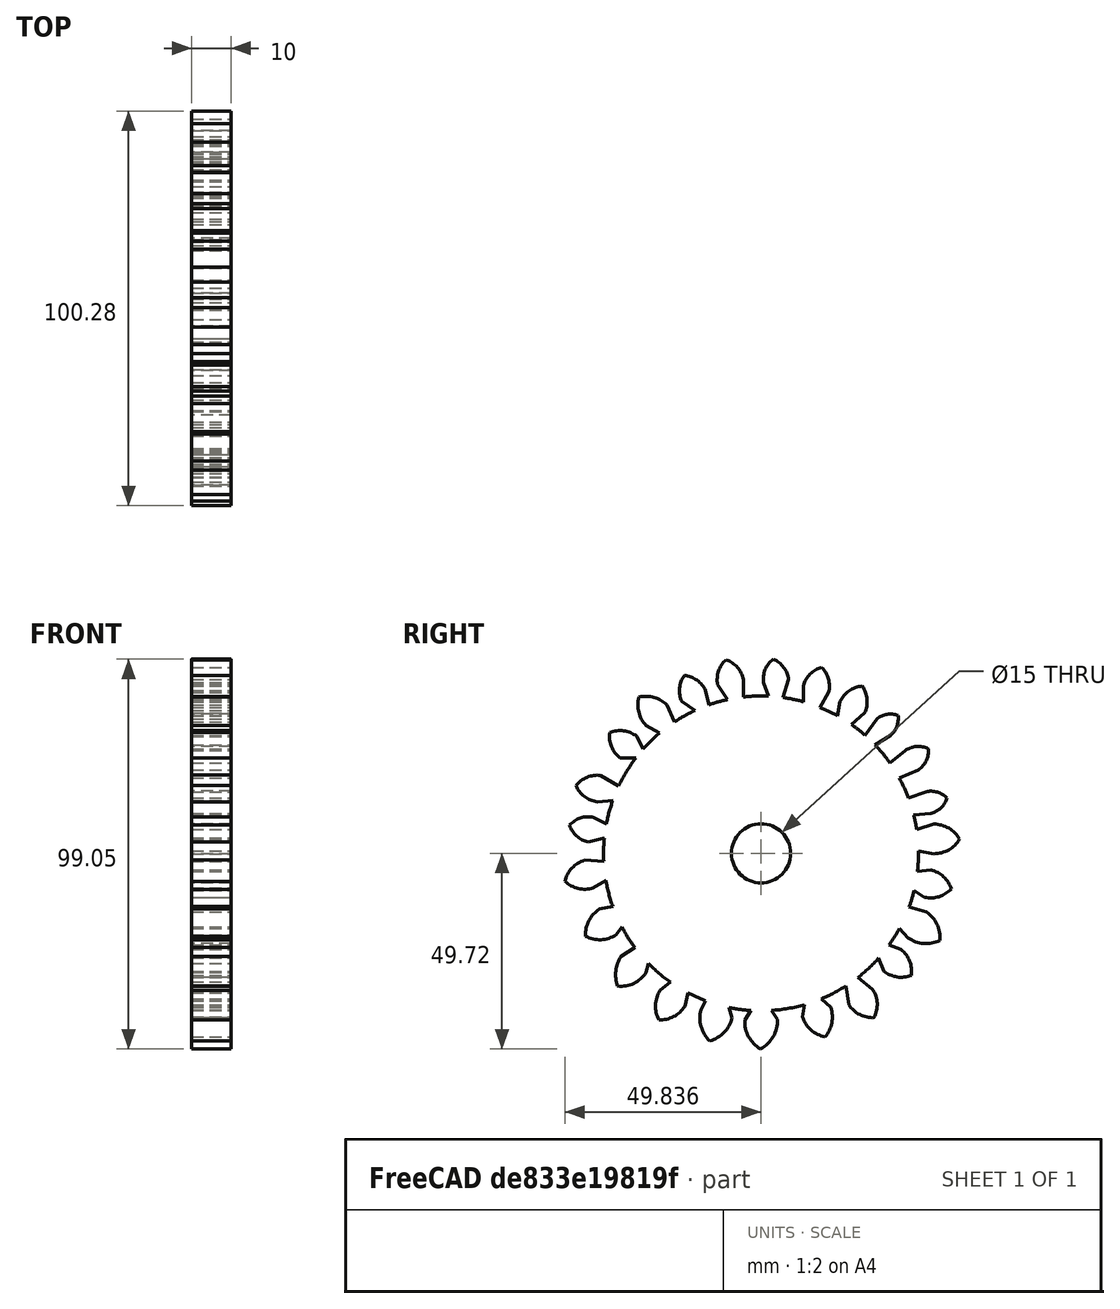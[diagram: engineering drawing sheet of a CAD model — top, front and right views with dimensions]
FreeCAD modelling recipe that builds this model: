
FCSTD DOCUMENT  (FreeCAD 0.21R33771 (Git))
Label: Machine Elment Design3
License: All rights reserved
LicenseURL: http://en.wikipedia.org/wiki/All_rights_reserved
objects: Sketcher::SketchObject×1, PartDesign::Pad×1, PartDesign::Body×1
note: 4 computed .brp shape members not serialized (recipe doc carries the construction recipe); baked Part::Feature solids carry a one-line shape summary decoded from their .brp

FEATURE [Sketcher::SketchObject] Sketch002
  FullyConstrained = false
  MapMode = 5
  Placement = pos=(0,0,0) rot=(0.57735,0.57735,0.57735;2.0944rad)
  Support = -> [YZ_Plane001]
  sketch-geometry (121):
    g0: Circle CenterX=-9.99419 CenterY=-0.180247 CenterZ=0 NormalX=0 NormalY=0 NormalZ=1 AngleXU=0 Radius=7.5
    g1: ArcOfCircle CenterX=-9.99419 CenterY=-0.180247 CenterZ=0 NormalX=0 NormalY=0 NormalZ=1 AngleXU=0 Radius=40 StartAngle=4.77797 EndAngle=4.99193
    g2: LineSegment StartX=4.94728 StartY=36.9244 StartZ=0 EndX=7.1719 EndY=40.7061 EndZ=0
    g3: LineSegment StartX=0.780338 StartY=38.3413 StartZ=0 EndX=0.755399 EndY=42.3758 EndZ=0
    g4: LineSegment StartX=-8.16746 StartY=39.778 StartZ=0 EndX=-9.38573 EndY=43.1826 EndZ=0
    g5: LineSegment StartX=-4.4803 StartY=39.4379 StartZ=0 EndX=-2.97992 EndY=44.0138 EndZ=0
    g6: LineSegment StartX=9.43345 StartY=34.785 StartZ=0 EndX=10.0579 EndY=38.368 EndZ=0
    g7: LineSegment StartX=12.9649 StartY=32.5746 StartZ=0 EndX=16.32 EndY=35.4471 EndZ=0
    g8: LineSegment StartX=16.4407 StartY=29.8397 StartZ=0 EndX=19.4768 EndY=34.0249 EndZ=0
    g9: LineSegment StartX=18.9896 StartY=27.3867 StartZ=0 EndX=22.8597 EndY=29.824 EndZ=0
    g10: LineSegment StartX=22.7265 StartY=22.8275 StartZ=0 EndX=26.6327 EndY=25.969 EndZ=0
    g11: LineSegment StartX=25.142 StartY=18.9364 StartZ=0 EndX=29.9678 EndY=21.0695 EndZ=0
    g12: LineSegment StartX=27.436 StartY=13.9257 StartZ=0 EndX=31.8669 EndY=15.4629 EndZ=0
    g13: LineSegment StartX=28.7806 StartY=9.64413 StartZ=0 EndX=33.1773 EndY=10.0099 EndZ=0
    g14: LineSegment StartX=29.5451 StartY=5.87322 StartZ=0 EndX=33.9689 EndY=7.25486 EndZ=0
    g15: LineSegment StartX=30.0003 StartY=0.485889 StartZ=0 EndX=33.9215 EndY=-0.257635 EndZ=0
    g16: LineSegment StartX=29.7446 StartY=-4.74416 StartZ=0 EndX=33.1412 EndY=-4.39115 EndZ=0
    g17: LineSegment StartX=28.8747 StartY=-9.62515 StartZ=0 EndX=31.5488 EndY=-11.3142 EndZ=0
    g18: LineSegment StartX=27.6371 StartY=-13.7408 StartZ=0 EndX=31.9739 EndY=-14.9902 EndZ=0
    g19: LineSegment StartX=25.1392 StartY=-19.3021 StartZ=0 EndX=27.3595 EndY=-21.6696 EndZ=0
    g20: LineSegment StartX=22.519 StartY=-23.4803 StartZ=0 EndX=25.6088 EndY=-24.633 EndZ=0
    g21: LineSegment StartX=19.8821 StartY=-26.7774 StartZ=0 EndX=21.2196 EndY=-30.1223 EndZ=0
    g22: LineSegment StartX=14.6541 StartY=-31.6836 StartZ=0 EndX=18.3711 EndY=-34.7285 EndZ=0
    g23: LineSegment StartX=11.6058 StartY=-33.8469 StartZ=0 EndX=12.3333 EndY=-38.6399 EndZ=0
    g24: LineSegment StartX=5.32297 StartY=-37.1314 StartZ=0 EndX=7.74528 EndY=-39.3474 EndZ=0
    g25: LineSegment StartX=1.04227 StartY=-38.6276 StartZ=0 EndX=0.551182 EndY=-41.7728 EndZ=0
    g26: LineSegment StartX=-18.1954 StartY=-39.3305 StartZ=0 EndX=-17.322 EndY=-41.9506 EndZ=0
    g27: LineSegment StartX=-24.0726 StartY=-37.6208 StartZ=0 EndX=-25.2906 EndY=-39.9483 EndZ=0
    g28: LineSegment StartX=-28.5263 StartY=-35.6283 StartZ=0 EndX=-29.3648 EndY=-39.0464 EndZ=0
    g29: LineSegment StartX=-33.0173 StartY=-32.8901 StartZ=0 EndX=-35.6372 EndY=-35.0452 EndZ=0
    g30: LineSegment StartX=-42.076 StartY=-24.0707 StartZ=0 EndX=-45.563 EndY=-26.3582 EndZ=0
    g31: LineSegment StartX=-45.3496 StartY=-18.8885 StartZ=0 EndX=-46.8081 EndY=-20.9017 EndZ=0
    g32: LineSegment StartX=-47.6402 StartY=-13.6999 StartZ=0 EndX=-50.9826 EndY=-14.2983 EndZ=0
    g33: LineSegment StartX=-49.4096 StartY=-6.99361 StartZ=0 EndX=-52.6314 EndY=-8.96467 EndZ=0
    g34: LineSegment StartX=-49.944 StartY=-2.18408 StartZ=0 EndX=-54.7931 EndY=-1.89974 EndZ=0
    g35: LineSegment StartX=-49.8015 StartY=3.7408 StartZ=0 EndX=-53.8673 EndY=2.70363 EndZ=0
    g36: LineSegment StartX=-49.2916 StartY=7.28397 StartZ=0 EndX=-52.5325 EndY=8.9854 EndZ=0
    g37: LineSegment StartX=-47.6693 StartY=13.258 StartZ=0 EndX=-51.6018 EndY=12.9345 EndZ=0
    g38: LineSegment StartX=-46.1533 StartY=16.9229 StartZ=0 EndX=-50.742 EndY=19.6321 EndZ=0
    g39: LineSegment StartX=-35.8355 StartY=30.3522 StartZ=0 EndX=-39.184 EndY=32.334 EndZ=0
    g40: LineSegment StartX=-31.9684 StartY=33.2433 StartZ=0 EndX=-33.8705 EndY=37.4981 EndZ=0
    g41: LineSegment StartX=-39.9365 StartY=26.3425 StartZ=0 EndX=-41.575 EndY=29.5668 EndZ=0
    g42: LineSegment StartX=-41.7916 StartY=24.0875 StartZ=0 EndX=-45.7975 EndY=24.0875 EndZ=0
    g43: LineSegment StartX=-26.7619 StartY=36.1356 StartZ=0 EndX=-30.1078 EndY=38.3785 EndZ=0
    g44: LineSegment StartX=-23.241 StartY=37.5626 StartZ=0 EndX=-24.0609 EndY=41.1716 EndZ=0
    g45: LineSegment StartX=-18.484 StartY=38.9084 StartZ=0 EndX=-21.0175 EndY=42.7184 EndZ=0
    g46: LineSegment StartX=-14.4903 StartY=39.5663 StartZ=0 EndX=-14.4903 EndY=43.9875 EndZ=0
    g47: ArcOfCircle CenterX=-9.38573 CenterY=43.1826 CenterZ=0 NormalX=0 NormalY=0 NormalZ=1 AngleXU=0 Radius=6.45951 StartAngle=0.129034 EndAngle=1.17623
    g48: ArcOfCircle CenterX=0.755399 CenterY=42.3758 CenterZ=0 NormalX=0 NormalY=0 NormalZ=1 AngleXU=0 Radius=6.63017 StartAngle=6.02862 EndAngle=7.07582
    g49: ArcOfCircle CenterX=10.0579 CenterY=38.368 CenterZ=0 NormalX=0 NormalY=0 NormalZ=1 AngleXU=0 Radius=6.90983 StartAngle=5.84675 EndAngle=6.89395
    g50: ArcOfCircle CenterX=19.4768 CenterY=34.0249 CenterZ=0 NormalX=0 NormalY=0 NormalZ=1 AngleXU=0 Radius=5.39369 StartAngle=5.39034 EndAngle=6.43754
    g51: ArcOfCircle CenterX=-21.0175 CenterY=42.7184 CenterZ=0 NormalX=0 NormalY=0 NormalZ=1 AngleXU=0 Radius=6.64951 StartAngle=0.192033 EndAngle=1.23923
    g52: ArcOfCircle CenterX=-30.1078 CenterY=38.3785 CenterZ=0 NormalX=0 NormalY=0 NormalZ=1 AngleXU=0 Radius=6.66085 StartAngle=0.43272 EndAngle=1.47992
    g53: ArcOfCircle CenterX=-39.184 CenterY=32.334 CenterZ=0 NormalX=0 NormalY=0 NormalZ=1 AngleXU=0 Radius=7.40955 StartAngle=0.77115 EndAngle=1.81835
    g54: ArcOfCircle CenterX=-45.7975 CenterY=24.0875 CenterZ=0 NormalX=0 NormalY=0 NormalZ=1 AngleXU=0 Radius=6.91758 StartAngle=0.914224 EndAngle=1.96142
    g55: ArcOfCircle CenterX=-51.6018 CenterY=12.9345 CenterZ=0 NormalX=0 NormalY=0 NormalZ=1 AngleXU=0 Radius=6.7525 StartAngle=1.44313 EndAngle=2.49033
    g56: ArcOfCircle CenterX=26.6327 CenterY=25.969 CenterZ=0 NormalX=0 NormalY=0 NormalZ=1 AngleXU=0 Radius=5.92692 StartAngle=5.31005 EndAngle=6.35725
    g57: ArcOfCircle CenterX=31.8669 CenterY=15.4629 CenterZ=0 NormalX=0 NormalY=0 NormalZ=1 AngleXU=0 Radius=5.60822 StartAngle=4.94823 EndAngle=5.99543
    g58: ArcOfCircle CenterX=33.9689 CenterY=7.25486 CenterZ=0 NormalX=0 NormalY=0 NormalZ=1 AngleXU=0 Radius=7.51265 StartAngle=4.70608 EndAngle=5.75328
    g59: ArcOfCircle CenterX=33.1412 CenterY=-4.39115 CenterZ=0 NormalX=0 NormalY=0 NormalZ=1 AngleXU=0 Radius=7.10381 StartAngle=4.4863 EndAngle=5.5335
    g60: ArcOfCircle CenterX=31.9739 CenterY=-14.9902 CenterZ=0 NormalX=0 NormalY=0 NormalZ=1 AngleXU=0 Radius=8.11826 StartAngle=4.10784 EndAngle=5.15504
    g61: ArcOfCircle CenterX=25.6088 CenterY=-24.633 CenterZ=0 NormalX=0 NormalY=0 NormalZ=1 AngleXU=0 Radius=7.02836 StartAngle=4.0379 EndAngle=5.0851
    g62: ArcOfCircle CenterX=18.3711 CenterY=-34.7285 CenterZ=0 NormalX=0 NormalY=0 NormalZ=1 AngleXU=0 Radius=7.19398 StartAngle=3.71643 EndAngle=4.76363
    g63: ArcOfCircle CenterX=-5.78085 CenterY=-42.7894 CenterZ=0 NormalX=0 NormalY=0 NormalZ=1 AngleXU=0 Radius=8.35625 StartAngle=3.11136 EndAngle=4.15955
    g64: ArcOfCircle CenterX=-17.322 CenterY=-41.9506 CenterZ=0 NormalX=0 NormalY=0 NormalZ=1 AngleXU=0 Radius=8.21631 StartAngle=2.89542 EndAngle=3.94262
    g65: ArcOfCircle CenterX=-29.3648 CenterY=-39.0464 CenterZ=0 NormalX=0 NormalY=0 NormalZ=1 AngleXU=0 Radius=7.43996 StartAngle=2.57377 EndAngle=3.62096
    g66: ArcOfCircle CenterX=-38.5302 CenterY=-30.9575 CenterZ=0 NormalX=0 NormalY=0 NormalZ=1 AngleXU=0 Radius=8.4032 StartAngle=2.56243 EndAngle=3.49802
    g67: ArcOfCircle CenterX=-46.8081 CenterY=-20.9017 CenterZ=0 NormalX=0 NormalY=0 NormalZ=1 AngleXU=0 Radius=7.8123 StartAngle=2.13454 EndAngle=3.18173
    g68: ArcOfCircle CenterX=-52.6314 CenterY=-8.96467 CenterZ=0 NormalX=0 NormalY=0 NormalZ=1 AngleXU=0 Radius=7.38824 StartAngle=1.86773 EndAngle=2.91493
    g69: ArcOfCircle CenterX=-53.8673 CenterY=2.70363 CenterZ=0 NormalX=0 NormalY=0 NormalZ=1 AngleXU=0 Radius=6.42202 StartAngle=1.36141 EndAngle=2.40861
    g70: LineSegment StartX=-38.6225 StartY=-28.1162 StartZ=0 EndX=-39.1898 EndY=-30.4587 EndZ=0
    g71: LineSegment StartX=-7.37288 StartY=-40.0943 StartZ=0 EndX=-5.77157 EndY=-42.3697 EndZ=0
    g72: LineSegment StartX=-12.554 StartY=-40.0983 StartZ=0 EndX=-14.1333 EndY=-42.5369 EndZ=0
    g73: ArcOfCircle CenterX=-9.99419 CenterY=-0.180247 CenterZ=0 NormalX=0 NormalY=0 NormalZ=1 AngleXU=0 Radius=40 StartAngle=5.10535 EndAngle=5.28282
    g74: ArcOfCircle CenterX=-9.99419 CenterY=-0.180247 CenterZ=0 NormalX=0 NormalY=0 NormalZ=1 AngleXU=0 Radius=40 StartAngle=5.37631 EndAngle=5.55579
    g75: ArcOfCircle CenterX=-9.99419 CenterY=-0.180247 CenterZ=0 NormalX=0 NormalY=0 NormalZ=1 AngleXU=0 Radius=40 StartAngle=5.66138 EndAngle=5.78476
    g76: ArcOfCircle CenterX=-9.99419 CenterY=-0.180247 CenterZ=0 NormalX=0 NormalY=0 NormalZ=1 AngleXU=0 Radius=40 StartAngle=5.93732 EndAngle=6.04481
    g77: ArcOfCircle CenterX=-9.99419 CenterY=-0.180247 CenterZ=0 NormalX=0 NormalY=0 NormalZ=1 AngleXU=0 Radius=40 StartAngle=6.16884 EndAngle=6.29984
    g78: ArcOfCircle CenterX=-9.99419 CenterY=-0.180247 CenterZ=0 NormalX=0 NormalY=0 NormalZ=1 AngleXU=0 Radius=40 StartAngle=1.29806 EndAngle=1.43251
    g79: ArcOfCircle CenterX=-9.99419 CenterY=-0.180247 CenterZ=0 NormalX=0 NormalY=0 NormalZ=1 AngleXU=0 Radius=40 StartAngle=1.06364 EndAngle=1.18798
    g80: ArcOfCircle CenterX=-9.99419 CenterY=-0.180247 CenterZ=0 NormalX=0 NormalY=0 NormalZ=1 AngleXU=0 Radius=40 StartAngle=1.52511 EndAngle=1.68344
    g81: ArcOfCircle CenterX=-9.99419 CenterY=-0.180247 CenterZ=0 NormalX=0 NormalY=0 NormalZ=1 AngleXU=0 Radius=40 StartAngle=1.78467 EndAngle=1.90834
    g82: ArcOfCircle CenterX=-9.99419 CenterY=-0.180247 CenterZ=0 NormalX=0 NormalY=0 NormalZ=1 AngleXU=0 Radius=40 StartAngle=0.848816 EndAngle=0.959442
    g83: ArcOfCircle CenterX=-9.99419 CenterY=-0.180247 CenterZ=0 NormalX=0 NormalY=0 NormalZ=1 AngleXU=0 Radius=40 StartAngle=0.612841 EndAngle=0.76035
    g84: ArcOfCircle CenterX=-9.99419 CenterY=-0.180247 CenterZ=0 NormalX=0 NormalY=0 NormalZ=1 AngleXU=0 Radius=40 StartAngle=0.360399 EndAngle=0.498281
    g85: ArcOfCircle CenterX=-9.99419 CenterY=-0.180247 CenterZ=0 NormalX=0 NormalY=0 NormalZ=1 AngleXU=0 Radius=40 StartAngle=0.15192 EndAngle=0.248148
    g86: ArcOfCircle CenterX=-9.99419 CenterY=-0.180247 CenterZ=0 NormalX=0 NormalY=0 NormalZ=1 AngleXU=0 Radius=40 StartAngle=4.5059 EndAngle=4.64835
    g87: ArcOfCircle CenterX=-9.99419 CenterY=-0.180247 CenterZ=0 NormalX=0 NormalY=0 NormalZ=1 AngleXU=0 Radius=40 StartAngle=4.23067 EndAngle=4.35272
    g88: ArcOfCircle CenterX=-9.99419 CenterY=-0.180247 CenterZ=0 NormalX=0 NormalY=0 NormalZ=1 AngleXU=0 Radius=40 StartAngle=3.91475 EndAngle=4.09908
    g89: ArcOfCircle CenterX=-9.99419 CenterY=-0.180247 CenterZ=0 NormalX=0 NormalY=0 NormalZ=1 AngleXU=0 Radius=40 StartAngle=3.62829 EndAngle=3.78168
    g90: ArcOfCircle CenterX=-9.99419 CenterY=-0.180247 CenterZ=0 NormalX=0 NormalY=0 NormalZ=1 AngleXU=0 Radius=40 StartAngle=3.31276 EndAngle=3.48637
    g91: ArcOfCircle CenterX=-9.99419 CenterY=-0.180247 CenterZ=0 NormalX=0 NormalY=0 NormalZ=1 AngleXU=0 Radius=40 StartAngle=3.04341 EndAngle=3.19171
    g92: ArcOfCircle CenterX=-9.99419 CenterY=-0.180247 CenterZ=0 NormalX=0 NormalY=0 NormalZ=1 AngleXU=0 Radius=40 StartAngle=2.79897 EndAngle=2.95389
    g93: ArcOfCircle CenterX=-9.99419 CenterY=-0.180247 CenterZ=0 NormalX=0 NormalY=0 NormalZ=1 AngleXU=0 Radius=40 StartAngle=2.4897 EndAngle=2.69978
    g94: ArcOfCircle CenterX=-9.99419 CenterY=-0.180247 CenterZ=0 NormalX=0 NormalY=0 NormalZ=1 AngleXU=0 Radius=40 StartAngle=2.27317 EndAngle=2.41668
    g95: ArcOfCircle CenterX=-9.99419 CenterY=-0.180247 CenterZ=0 NormalX=0 NormalY=0 NormalZ=1 AngleXU=0 Radius=40 StartAngle=2.00335 EndAngle=2.15239
    g96: ArcOfCircle CenterX=7.74528 CenterY=-39.3474 CenterZ=0 NormalX=0 NormalY=0 NormalZ=1 AngleXU=0 Radius=7.59194 StartAngle=3.46676 EndAngle=4.51396
    g97: ArcOfCircle CenterX=-24.0609 CenterY=41.1716 CenterZ=0 NormalX=0 NormalY=0 NormalZ=1 AngleXU=0 Radius=6.66085 StartAngle=2.52712 EndAngle=3.57431
    g98: ArcOfCircle CenterX=-14.4903 CenterY=43.9875 CenterZ=0 NormalX=0 NormalY=0 NormalZ=1 AngleXU=0 Radius=6.64951 StartAngle=2.28643 EndAngle=3.33363
    g99: ArcOfCircle CenterX=-2.97992 CenterY=44.0138 CenterZ=0 NormalX=0 NormalY=0 NormalZ=1 AngleXU=0 Radius=6.45951 StartAngle=2.22343 EndAngle=3.27063
    g100: ArcOfCircle CenterX=7.1719 CenterY=40.7061 CenterZ=0 NormalX=0 NormalY=0 NormalZ=1 AngleXU=0 Radius=6.63017 StartAngle=1.83983 EndAngle=2.88703
    g101: ArcOfCircle CenterX=16.32 CenterY=35.4471 CenterZ=0 NormalX=0 NormalY=0 NormalZ=1 AngleXU=0 Radius=6.90983 StartAngle=1.65796 EndAngle=2.70516
    g102: ArcOfCircle CenterX=22.8597 CenterY=29.824 CenterZ=0 NormalX=0 NormalY=0 NormalZ=1 AngleXU=0 Radius=5.39369 StartAngle=1.20155 EndAngle=2.24875
    g103: ArcOfCircle CenterX=29.9678 CenterY=21.0695 CenterZ=0 NormalX=0 NormalY=0 NormalZ=1 AngleXU=0 Radius=5.92692 StartAngle=1.12126 EndAngle=2.16846
    g104: ArcOfCircle CenterX=33.1773 CenterY=10.0099 CenterZ=0 NormalX=0 NormalY=0 NormalZ=1 AngleXU=0 Radius=5.60822 StartAngle=0.75944 EndAngle=1.80664
    g105: ArcOfCircle CenterX=33.9215 CenterY=-0.257635 CenterZ=0 NormalX=0 NormalY=0 NormalZ=1 AngleXU=0 Radius=7.51265 StartAngle=0.517294 EndAngle=1.56449
    g106: ArcOfCircle CenterX=31.5488 CenterY=-11.3142 CenterZ=0 NormalX=0 NormalY=0 NormalZ=1 AngleXU=0 Radius=7.10381 StartAngle=0.297513 EndAngle=1.34471
    g107: ArcOfCircle CenterX=27.3595 CenterY=-21.6696 CenterZ=0 NormalX=0 NormalY=0 NormalZ=1 AngleXU=0 Radius=8.11826 StartAngle=6.20224 EndAngle=7.24944
    g108: ArcOfCircle CenterX=21.2196 CenterY=-30.1223 CenterZ=0 NormalX=0 NormalY=0 NormalZ=1 AngleXU=0 Radius=7.02836 StartAngle=6.1323 EndAngle=7.1795
    g109: ArcOfCircle CenterX=12.3333 CenterY=-38.6399 CenterZ=0 NormalX=0 NormalY=0 NormalZ=1 AngleXU=0 Radius=7.19398 StartAngle=5.81083 EndAngle=6.85802
    g110: ArcOfCircle CenterX=0.551182 CenterY=-41.7728 CenterZ=0 NormalX=0 NormalY=0 NormalZ=1 AngleXU=0 Radius=7.59194 StartAngle=5.56116 EndAngle=6.60836
    g111: ArcOfCircle CenterX=-14.1333 CenterY=-42.5369 CenterZ=0 NormalX=0 NormalY=0 NormalZ=1 AngleXU=0 Radius=8.36339 StartAngle=5.20625 EndAngle=6.30317
    g112: ArcOfCircle CenterX=-25.2906 CenterY=-39.9483 CenterZ=0 NormalX=0 NormalY=0 NormalZ=1 AngleXU=0 Radius=8.21631 StartAngle=4.98982 EndAngle=6.03702
    g113: ArcOfCircle CenterX=-35.6372 CenterY=-35.0452 CenterZ=0 NormalX=0 NormalY=0 NormalZ=1 AngleXU=0 Radius=7.43996 StartAngle=4.66816 EndAngle=5.71536
    g114: ArcOfCircle CenterX=-45.563 CenterY=-26.3582 CenterZ=0 NormalX=0 NormalY=0 NormalZ=1 AngleXU=0 Radius=7.57838 StartAngle=4.60102 EndAngle=5.71147
    g115: ArcOfCircle CenterX=-50.9826 CenterY=-14.2983 CenterZ=0 NormalX=0 NormalY=0 NormalZ=1 AngleXU=0 Radius=7.8123 StartAngle=4.22893 EndAngle=5.27613
    g116: ArcOfCircle CenterX=-54.7931 CenterY=-1.89974 CenterZ=0 NormalX=0 NormalY=0 NormalZ=1 AngleXU=0 Radius=7.38824 StartAngle=3.96212 EndAngle=5.00932
    g117: ArcOfCircle CenterX=-33.8705 CenterY=37.4981 CenterZ=0 NormalX=0 NormalY=0 NormalZ=1 AngleXU=0 Radius=7.40955 StartAngle=2.86554 EndAngle=3.91274
    g118: ArcOfCircle CenterX=-41.575 CenterY=29.5668 CenterZ=0 NormalX=0 NormalY=0 NormalZ=1 AngleXU=0 Radius=6.91758 StartAngle=3.00862 EndAngle=4.05582
    g119: ArcOfCircle CenterX=-50.742 CenterY=19.6321 CenterZ=0 NormalX=0 NormalY=0 NormalZ=1 AngleXU=0 Radius=6.7525 StartAngle=3.53752 EndAngle=4.58472
    g120: ArcOfCircle CenterX=-52.5325 CenterY=8.9854 CenterZ=0 NormalX=0 NormalY=0 NormalZ=1 AngleXU=0 Radius=6.42202 StartAngle=3.45581 EndAngle=4.50301
  constraints (261):
    c: Diameter(g0) = 15
    c: Coincident(g1,g0)
    c: Diameter(g1) = 80
    c: PointOnObject(g2,g1)
    c: PointOnObject(g3,g1)
    c: PointOnObject(g4,g1)
    c: PointOnObject(g5,g1)
    c: PointOnObject(g6,g1)
    c: PointOnObject(g7,g1)
    c: PointOnObject(g8,g1)
    c: PointOnObject(g9,g1)
    c: PointOnObject(g10,g1)
    c: PointOnObject(g11,g1)
    c: PointOnObject(g12,g1)
    c: PointOnObject(g13,g1)
    c: PointOnObject(g14,g1)
    c: PointOnObject(g15,g1)
    c: PointOnObject(g16,g1)
    c: PointOnObject(g17,g1)
    c: PointOnObject(g18,g1)
    c: PointOnObject(g19,g1)
    c: PointOnObject(g20,g1)
    c: PointOnObject(g21,g1)
    c: PointOnObject(g22,g1)
    c: PointOnObject(g23,g1)
    c: PointOnObject(g26,g1)
    c: PointOnObject(g27,g1)
    c: PointOnObject(g28,g1)
    c: PointOnObject(g29,g1)
    c: PointOnObject(g30,g1)
    c: PointOnObject(g31,g1)
    c: PointOnObject(g32,g1)
    c: PointOnObject(g33,g1)
    c: PointOnObject(g34,g1)
    c: PointOnObject(g35,g1)
    c: PointOnObject(g36,g1)
    c: PointOnObject(g37,g1)
    c: PointOnObject(g38,g1)
    c: PointOnObject(g39,g1)
    c: PointOnObject(g40,g1)
    c: PointOnObject(g41,g1)
    c: PointOnObject(g42,g1)
    c: Horizontal(g42)
    c: PointOnObject(g43,g1)
    c: PointOnObject(g44,g1)
    c: PointOnObject(g45,g1)
    c: PointOnObject(g46,g1)
    c: Vertical(g46)
    c: Coincident(g47,g4)
    c: Coincident(g47,g5)
    c: Coincident(g48,g3)
    c: Coincident(g48,g2)
    c: Coincident(g49,g6)
    c: Coincident(g49,g7)
    c: Coincident(g50,g8)
    c: Coincident(g50,g9)
    c: Coincident(g51,g45)
    c: Coincident(g51,g46)
    c: Coincident(g52,g43)
    c: Coincident(g52,g44)
    c: Coincident(g53,g39)
    c: Coincident(g53,g40)
    c: Coincident(g54,g42)
    c: Coincident(g54,g41)
    c: Coincident(g55,g37)
    c: Coincident(g55,g38)
    c: Coincident(g56,g10)
    c: Coincident(g56,g11)
    c: Coincident(g57,g12)
    c: Coincident(g57,g13)
    c: Coincident(g58,g14)
    c: Coincident(g58,g15)
    c: Coincident(g59,g16)
    c: Coincident(g59,g17)
    c: Coincident(g60,g18)
    c: Coincident(g60,g19)
    c: Coincident(g61,g20)
    c: Coincident(g61,g21)
    c: Coincident(g62,g22)
    c: Coincident(g62,g23)
    c: Coincident(g64,g26)
    c: Coincident(g64,g27)
    c: Coincident(g65,g28)
    c: Coincident(g65,g29)
    c: Coincident(g66,g30)
    c: Coincident(g67,g31)
    c: Coincident(g67,g32)
    c: Coincident(g68,g33)
    c: Coincident(g68,g34)
    c: Coincident(g69,g35)
    c: Coincident(g69,g36)
    c: PointOnObject(g70,g1)
    c: Coincident(g72,g63)
    c: Coincident(g86,g72)
    c: Coincident(g1,g71)
    c: Equal(g1,g73)
    c: Coincident(g1,g25)
    c: Coincident(g73,g24)
    c: Coincident(g1,g73)
    c: Equal(g73,g74)
    c: PointOnObject(g73,g23)
    c: PointOnObject(g74,g22)
    c: Coincident(g73,g74)
    c: Equal(g74,g75)
    c: PointOnObject(g74,g21)
    c: PointOnObject(g75,g20)
    c: Coincident(g74,g75)
    c: Equal(g75,g76)
    c: PointOnObject(g75,g19)
    c: PointOnObject(g76,g18)
    c: Coincident(g75,g76)
    c: Equal(g76,g77)
    c: PointOnObject(g76,g17)
    c: PointOnObject(g77,g16)
    c: Coincident(g76,g77)
    c: Equal(g77,g78)
    c: PointOnObject(g79,g2)
    c: PointOnObject(g78,g3)
    c: Coincident(g77,g78)
    c: Equal(g77,g79)
    c: PointOnObject(g82,g7)
    c: PointOnObject(g79,g6)
    c: Coincident(g77,g79)
    c: Equal(g78,g80)
    c: PointOnObject(g78,g5)
    c: PointOnObject(g80,g4)
    c: Coincident(g78,g80)
    c: Equal(g80,g81)
    c: PointOnObject(g80,g46)
    c: PointOnObject(g81,g45)
    c: Coincident(g80,g81)
    c: Equal(g77,g82)
    c: PointOnObject(g83,g9)
    c: PointOnObject(g82,g8)
    c: Coincident(g77,g82)
    c: Equal(g77,g83)
    c: PointOnObject(g84,g11)
    c: PointOnObject(g83,g10)
    c: Coincident(g77,g83)
    c: Equal(g77,g84)
    c: PointOnObject(g85,g13)
    c: PointOnObject(g84,g12)
    c: Coincident(g77,g84)
    c: Equal(g77,g85)
    c: PointOnObject(g77,g15)
    c: PointOnObject(g85,g14)
    c: Coincident(g77,g85)
    c: Equal(g81,g86)
    c: PointOnObject(g87,g27)
    c: PointOnObject(g86,g26)
    c: Coincident(g81,g86)
    c: Equal(g81,g87)
    c: PointOnObject(g88,g29)
    c: PointOnObject(g87,g28)
    c: Coincident(g81,g87)
    c: Equal(g81,g88)
    c: PointOnObject(g89,g30)
    c: PointOnObject(g88,g70)
    c: Coincident(g81,g88)
    c: Equal(g81,g89)
    c: PointOnObject(g90,g32)
    c: PointOnObject(g89,g31)
    c: Coincident(g81,g89)
    c: Equal(g81,g90)
    c: PointOnObject(g91,g34)
    c: PointOnObject(g90,g33)
    c: Coincident(g81,g90)
    c: Equal(g81,g91)
    c: PointOnObject(g92,g36)
    c: PointOnObject(g91,g35)
    c: Coincident(g81,g91)
    c: Equal(g81,g92)
    c: PointOnObject(g93,g38)
    c: PointOnObject(g92,g37)
    c: Coincident(g81,g92)
    c: Equal(g81,g93)
    c: PointOnObject(g94,g41)
    c: PointOnObject(g93,g42)
    c: Coincident(g81,g93)
    c: Equal(g81,g94)
    c: PointOnObject(g95,g40)
    c: PointOnObject(g94,g39)
    c: Coincident(g81,g94)
    c: Equal(g81,g95)
    c: PointOnObject(g81,g44)
    c: PointOnObject(g95,g43)
    c: Coincident(g81,g95)
    c: Coincident(g96,g24)
    c: Coincident(g96,g25)
    c: Coincident(g97,g44)
    c: Coincident(g97,g52)
    c: Coincident(g97,g43)
    c: Coincident(g98,g46)
    c: Coincident(g98,g51)
    c: Coincident(g98,g45)
    c: Coincident(g99,g5)
    c: Coincident(g99,g47)
    c: Coincident(g99,g4)
    c: Coincident(g100,g2)
    c: Coincident(g100,g48)
    c: Coincident(g100,g3)
    c: Coincident(g101,g7)
    c: Coincident(g101,g49)
    c: Coincident(g101,g6)
    c: Coincident(g102,g9)
    c: Coincident(g102,g50)
    c: Coincident(g102,g8)
    c: Coincident(g103,g11)
    c: Coincident(g103,g56)
    c: Coincident(g103,g10)
    c: Coincident(g104,g13)
    c: Coincident(g104,g57)
    c: Coincident(g104,g12)
    c: Coincident(g105,g15)
    c: Coincident(g105,g58)
    c: Coincident(g105,g14)
    c: Coincident(g106,g17)
    c: Coincident(g106,g59)
    c: Coincident(g106,g16)
    c: Coincident(g107,g19)
    c: Coincident(g107,g60)
    c: Coincident(g107,g18)
    c: Coincident(g108,g21)
    c: Coincident(g108,g61)
    c: Coincident(g108,g20)
    c: Coincident(g109,g23)
    c: Coincident(g109,g62)
    c: Coincident(g109,g22)
    c: Coincident(g110,g25)
    c: Coincident(g110,g96)
    c: Coincident(g110,g24)
    c: Coincident(g111,g63)
    c: Coincident(g111,g63)
    c: Coincident(g111,g71)
    c: Coincident(g112,g27)
    c: Coincident(g112,g64)
    c: Coincident(g112,g26)
    c: Coincident(g113,g29)
    c: Coincident(g113,g65)
    c: Coincident(g113,g28)
    c: Coincident(g114,g30)
    c: Coincident(g114,g66)
    c: Coincident(g114,g70)
    c: Coincident(g115,g32)
    c: Coincident(g115,g67)
    c: Coincident(g115,g31)
    c: Coincident(g116,g34)
    c: Coincident(g116,g68)
    c: Coincident(g116,g33)
    c: Coincident(g117,g40)
    c: Coincident(g117,g53)
    c: Coincident(g117,g39)
    c: Coincident(g118,g41)
    c: Coincident(g118,g54)
    c: Coincident(g118,g42)
    c: Coincident(g119,g38)
    c: Coincident(g119,g55)
    c: Coincident(g119,g37)
    c: Coincident(g120,g36)
    c: Coincident(g120,g69)
    c: Coincident(g120,g35)
FEATURE [PartDesign::Pad] Pad001
  Direction = (1,-2e-16,3e-16)
  Length = 10
  Length2 = 10
  Placement = pos=(0,0,0) rot=(0.57735,0.57735,0.57735;2.0944rad)
  Profile = -> Sketch002
  ReferenceAxis = -> Sketch002 [N_Axis]
  Type = 0
FEATURE [PartDesign::Body] Body001  label="Spur Gear"
  Group = -> [Sketch002,Pad001]
  Origin = -> Origin001
  Placement = pos=(496,-1216,-128) rot=(0,0,1;0rad)
  Tip = -> Pad001
